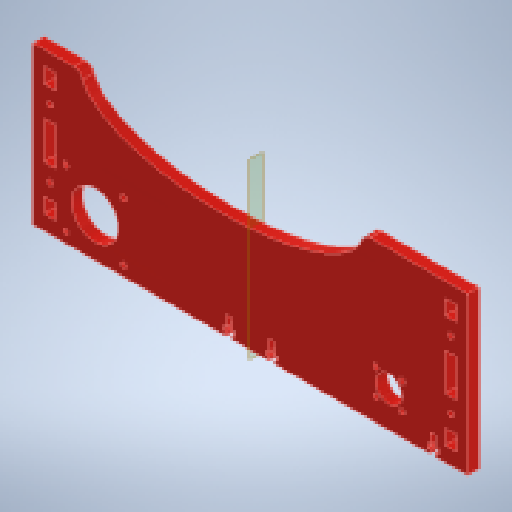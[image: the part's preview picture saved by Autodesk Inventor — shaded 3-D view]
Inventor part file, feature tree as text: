
AUTODESK INVENTOR PART (.ipt)
format: ipt  version: 2024.2 (Build 282272000, 272)  size: 492,544 bytes
history: native  units: mm
features: extrude x6, sketch x6, other x2, fillet x1, mirror x1, projected_geometry x1
ambient origin geometry x8: Origin, YZ Plane, XZ Plane, XY Plane, X Axis, Y Axis, Z Axis, Center Point
bodies: Body1 (feature_tree)
feature tree (17):
  other  "Твердое тело1"
  extrude  "Выдавливание1"  Depth=6.0mm TaperAngle=0.0deg
  extrude  "Выдавливание2"  Depth=6.0mm
  other  "РабПлоскость1"
  extrude  "Выдавливание3"  Depth=8.0mm
  fillet  "Сопряжение1"  Radius=8.0mm
  extrude  "Выдавливание4"  Depth=8.0mm
  extrude  "Выдавливание5"  Depth=84.0mm
  mirror  "Зеркальное отражение2"
  extrude  "Выдавливание6"  Depth=42.0mm
  sketch  "Эскиз1"
  sketch  "Эскиз2"
  sketch  "Эскиз5"
  sketch  "Эскиз6"
  sketch  "Эскиз7"
  sketch  "Эскиз8"
  projected_geometry  "Спроецированная петля1"
